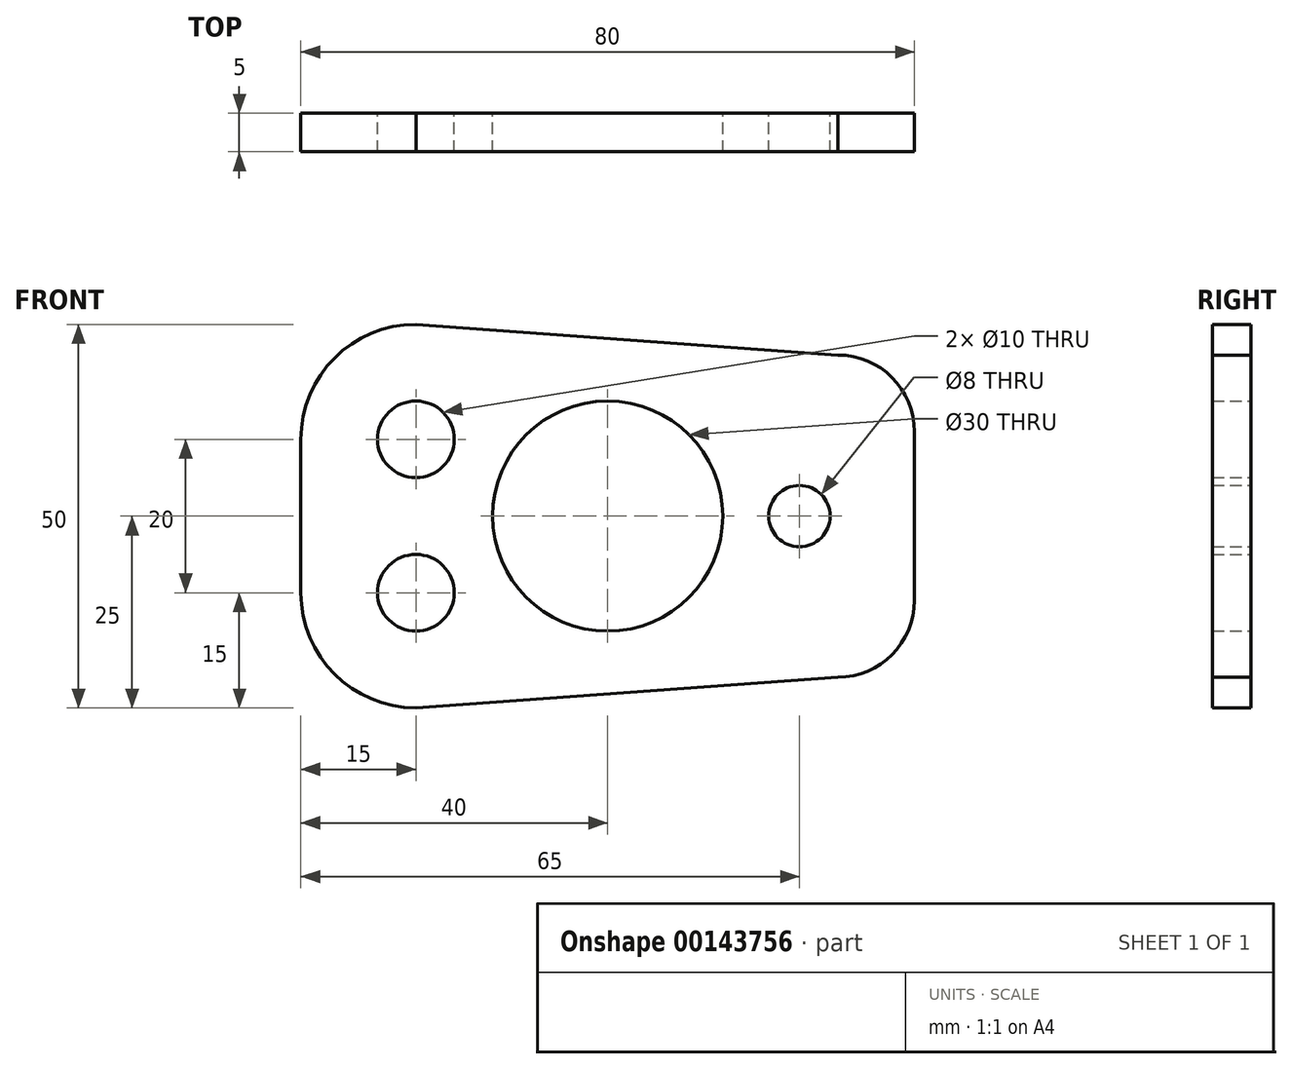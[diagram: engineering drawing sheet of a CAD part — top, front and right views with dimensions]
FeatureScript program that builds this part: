
annotation { "Feature Type Name" : "Feature", "Feature Type Description" : "" }
export const myFeature = defineFeature(function(context is Context, id is Id, definition is map)
    precondition{}
    {
        {
            var Q0;
            Q0=qCreatedBy(makeId("Front.planeOp"),FACE);
            var sketch = newSketch(context, id + "F0", { "sketchPlane" : qUnion([Q0])});
            skCircle(sketch, "E0", {"center": v(0, 0) * mm, "radius": 15 * mm});
            skCircle(sketch, "E1", {"center": v(25, 0) * mm, "radius": 4 * mm});
            skLineSegment(sketch, "E2", {"start": v(-59.43, 0) * mm, "end": v(101.23, 0) * mm, "construction": true});
            skLineSegment(sketch, "E3", {"start": v(-25, -28.52) * mm, "end": v(-25, 34.79) * mm, "construction": true});
            skLineSegment(sketch, "E4", {"start": v(0, -26.86) * mm, "end": v(0, 36.66) * mm, "construction": true});
            skLineSegment(sketch, "E5", {"start": v(-40, 0) * mm, "end": v(-40, 10) * mm});
            skLineSegment(sketch, "E6", {"start": v(-40, 0) * mm, "end": v(-40, -10) * mm});
            skLineSegment(sketch, "E7", {"start": v(40, 0) * mm, "end": v(40, 11) * mm});
            skLineSegment(sketch, "E8", {"start": v(40, 0) * mm, "end": v(40, -11) * mm});
            skCircle(sketch, "E9", {"center": v(-25, 10) * mm, "radius": 5 * mm});
            skCircle(sketch, "E10", {"center": v(-25, -10) * mm, "radius": 5 * mm});
            skLineSegment(sketch, "E11", {"start": v(-40, -10) * mm, "end": v(-20, -10) * mm, "construction": true});
            skLineSegment(sketch, "E12", {"start": v(-40, 10) * mm, "end": v(-20, 10) * mm, "construction": true});
            skArc(sketch, "E13", {"start": v(-40, 10) * mm, "mid": v(-35.6, 20.6) * mm, "end": v(-25, 25) * mm});
            skLineSegment(sketch, "E14", {"start": v(25, -10.27) * mm, "end": v(25, 43.57) * mm, "construction": true});
            skArc(sketch, "E15", {"start": v(-40, -10) * mm, "mid": v(-35.6, -20.6) * mm, "end": v(-25, -25) * mm});
            skArc(sketch, "E16", {"start": v(40, 11) * mm, "mid": v(37.07, 18.07) * mm, "end": v(30, 21) * mm});
            skArc(sketch, "E17", {"start": v(40, -11) * mm, "mid": v(37.07, -18.07) * mm, "end": v(30, -21) * mm});
            skLineSegment(sketch, "E18", {"start": v(-25, 25) * mm, "end": v(30, 21) * mm});
            skLineSegment(sketch, "E19", {"start": v(-25, -25) * mm, "end": v(30, -21) * mm});
            skSolve(sketch);
        }
        {
            var Q0;
            Q0=qSketchRegion(id+"F0",true);
            extrude(context, id + "F1", {"entities" : qUnion([Q0]), "depth" : 5 * mm});
        }
    });
